# Revit family: Magnuson-Stilla-Outdoor_Tables
name_source: partatom
category: Furniture
units: mm (PartAtom-declared; Revit-internal decimal feet)

## family parameters
Always vertical = Yes
Cut with Voids When Loaded = No
OmniClass Number = 23.40.20.00
OmniClass Title = General Furniture and Specialties
Room Calculation Point = No
Shared = No
Work Plane-Based = No

## types (2) — shared parameters
Assembly Code = E2020200
Default Elevation = 0"
Height = 28 7/16"
Keynote = 12500
Leg Finish = MAG - Painted White
Manufacturer = Magnuson Group
Product Documentation Link = https://magnusongroup.com
Revit Model Built By = https://www.servex-us.com
Top Finish = MAG - Painted White
Type Comments = Stilla Table
URL = www.magnusongroup.com

## per-type parameters (varying)
| type | Depth | Description | Leg R | Leg S | Sustainability | Top R | Top S | Width |
| STILTBL-S | 28 3/4" | Fiberglass filled polypropylene table with square top and 4 legs with rubber feet. Six tables can be stacked vertically for storage. Ships unassembled. Suitable for indoor and outdoor use. | No | Yes |  | No | Yes | 28 3/4" |
| STILTBL-R | 32 1/2" | Fiberglass filled polypropylene table with round top and 4 legs with rubber feet. Six tables can be stacked vertically for storage. Ships unassembled. Suitable for indoor and outdoor use. | Yes | No | https://magnusongroup.com | Yes | No | 32 1/2" |

note: column(s) folded — value = type name in every type: Model

## geometry (parser evidence)
native form markers: Sweep x8
no freeform markers — native parametric forms only
